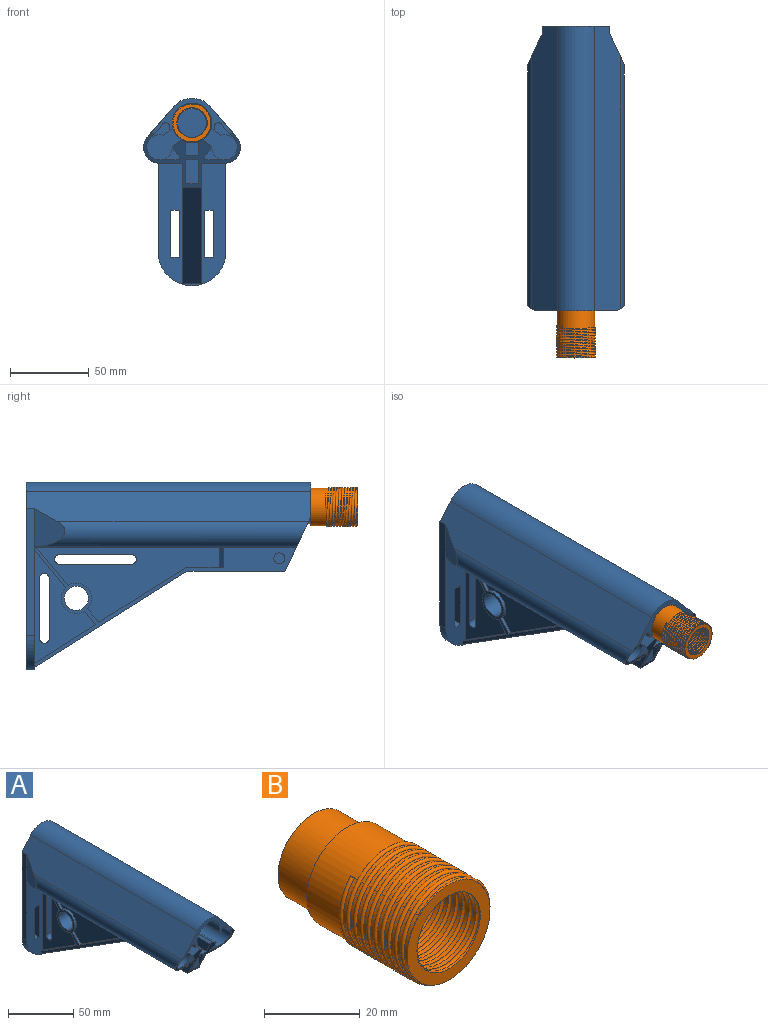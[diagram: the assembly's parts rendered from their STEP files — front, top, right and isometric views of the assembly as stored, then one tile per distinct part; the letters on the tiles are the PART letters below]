
ASSEMBLY  parts=2 mates=1
PART A: 102 faces, bbox 61.2x180.1x118.6 mm
  f0: plane 77.59x43mm, normal (0,-1,0), area 2194mm2, adj f4,f8,f9,f10,f11,f12,f15,f23
  f1: plane 118.58x43mm, normal (0,1,0), area 4330mm2, adj f13,f14,f22,f23,f24,f25,f94,f95
  f2: plane 8.42x6.86mm, normal (0,0.78,-0.63), area 21.7mm2, adj f9,f33,f34,f68
  f3: plane 8.58x7.16mm, normal (0,-0.77,0.64), area 22.3mm2, adj f9,f37,f39,f67
  f4: plane 24.44x19.89mm, normal (0,0.78,-0.63), area 63mm2, adj f0,f8,f42,f66
  f5: plane 24.33x20.29mm, normal (0,-0.77,0.64), area 63.4mm2, adj f8,f10,f47,f65
  f6: plane 61.22x34.25mm, normal (0,-0.9,-0.43), area 463mm2, adj f7,f8,f9,f10,f11,f12,f13,f14
  f7: cylinder r=8mm len=148.25mm, axis (0,1,0), area 5825.9mm2, adj f6,f48,f51,f55,f56,f88,f89
  f8: plane 166.01x76.2mm, normal (-1,0,0), area 1146.1mm2, adj f0,f4,f5,f6,f10,f21,f31,f40
  f9: plane 166.01x76.2mm, normal (1,0,0), area 1184.3mm2, adj f0,f2,f3,f6,f11,f21,f31,f32
  f10: plane 166.01x16.61mm, normal (0,0,-1), area 2659.9mm2, adj f0,f5,f6,f8,f15,f47,f91
  f11: plane 166.01x16.61mm, normal (0,0,-1), area 2659.9mm2, adj f0,f6,f9,f12,f38,f39,f90
  f12: cylinder r=10mm len=173.87mm, axis (0,1,0), area 3544.9mm2, adj f0,f6,f11,f13,f29
  f13: plane 180.08x18.88mm, normal (0.76,0,0.65), area 4349.5mm2, adj f1,f6,f12,f20,f22,f25,f29,f30
  f14: plane 180.08x18.88mm, normal (-0.76,0,0.65), area 4349.5mm2, adj f1,f6,f15,f20,f22,f24,f27
  f15: cylinder r=10mm len=173.87mm, axis (0,1,0), area 3544.9mm2, adj f0,f6,f10,f14,f27
  f16: plane 172.59x8.74mm, normal (1,0,0), area 1490.5mm2, adj f6,f17,f19,f26
  f17: cylinder r=12.25mm len=175mm, axis (0,1,0), area 9267mm2, adj f6,f16,f18,f20,f26,f48,f50,f86
  f18: plane 172.59x8.74mm, normal (-1,0,0), area 1490.5mm2, adj f6,f17,f19,f26
  f19: plane 168.43x8mm, normal (0,0,1), area 1299.7mm2, adj f6,f16,f18,f26,f72
  f20: plane 52.33x22.14mm, normal (0,-1,0), area 237.4mm2, adj f6,f13,f14,f17,f22,f54,f55,f57
  f21: plane 61.93x12mm, normal (0,0,-1), area 730.6mm2, adj f6,f8,f9,f31,f70
  f22: cylinder r=15.63mm len=180.08mm, axis (0,1,0), area 4940.3mm2, adj f1,f13,f14,f20
  f23: cylinder r=21.5mm len=43mm, axis (0,-1,0), area 343.1mm2, adj f0,f1,f24,f25
  f24: plane 80.38x5.08mm, normal (-1,0,0), area 408.3mm2, adj f0,f1,f14,f23,f27
  f25: plane 80.38x5.08mm, normal (1,0,0), area 404.2mm2, adj f0,f1,f13,f23,f28,f30
  f26: plane 32.57x24.5mm, normal (0,-1,0), area 537.8mm2, adj f16,f17,f18,f19
  f27: plane 24.29x19.54mm, normal (-0.91,0.42,0), area 355.4mm2, adj f14,f15,f24
  f28: plane 0.17x0.07mm, normal (0,0,1), area 0mm2, adj f25,f29,f30
  f29: plane 24.4x19.68mm, normal (0.91,0.42,0), area 359.2mm2, adj f0,f12,f13,f28,f30
  f30: plane 24.4x0.07mm, normal (0.42,-0.91,0), area 1.8mm2, adj f13,f25,f28,f29
  f31: plane 96.76x60.84mm, normal (0,-0.53,-0.85), area 1371.6mm2, adj f0,f8,f9,f21
  f32: plane 24.44x19.89mm, normal (0,0.78,-0.63), area 63mm2, adj f0,f9,f34,f68
  f33: plane 38.85x24.67mm, normal (0,0.54,0.84), area 92mm2, adj f0,f2,f9,f34
  f34: plane 72.39x38.85mm, normal (1,0,0), area 1021.4mm2, adj f0,f2,f32,f33,f68,f77,f78,f79
  f35: plane 22.84x2mm, normal (0,0,1), area 43.7mm2, adj f9,f36,f39,f90
  f36: plane 16.91x10.14mm, normal (0,0.51,0.86), area 39.4mm2, adj f9,f35,f37,f39
  f37: plane 38.85x24.67mm, normal (0,0.54,0.84), area 92mm2, adj f3,f9,f36,f39
  f38: plane 24.33x20.29mm, normal (0,-0.77,0.64), area 63.4mm2, adj f9,f11,f39,f67
  f39: plane 116.33x47.63mm, normal (1,0,0), area 2452.7mm2, adj f3,f11,f35,f36,f37,f38,f67,f73
  f40: plane 38.85x24.67mm, normal (0,0.54,0.84), area 92mm2, adj f0,f8,f41,f42
  f41: plane 8.42x6.86mm, normal (0,0.78,-0.63), area 21.7mm2, adj f8,f40,f42,f66
  f42: plane 72.39x38.85mm, normal (-1,0,0), area 1021.4mm2, adj f0,f4,f40,f41,f66,f77,f78,f79
  f43: plane 38.85x24.67mm, normal (0,0.54,0.84), area 92mm2, adj f8,f44,f46,f47
  f44: plane 16.91x10.14mm, normal (0,0.51,0.86), area 39.4mm2, adj f8,f43,f45,f47
  f45: plane 22.84x2mm, normal (0,0,1), area 43.7mm2, adj f8,f44,f47,f91
  f46: plane 8.58x7.16mm, normal (0,-0.77,0.64), area 22.3mm2, adj f8,f43,f47,f65
  f47: plane 116.33x47.63mm, normal (-1,0,0), area 2452.7mm2, adj f5,f10,f43,f44,f45,f46,f65,f73
  f48: plane 22.18x20.19mm, normal (0,-1,0), area 256.9mm2, adj f7,f17,f88,f89
  f49: cylinder r=8mm len=148.25mm, axis (0,1,0), area 5825.9mm2, adj f6,f50,f58,f61,f63,f86,f87
  f50: plane 22.18x20.19mm, normal (0,-1,0), area 256.9mm2, adj f17,f49,f86,f87
  f51: plane 12.79x10.33mm, normal (0,-1,0), area 49.1mm2, adj f7,f54,f55,f57,f88
  f52: plane 2.49x1.18mm, normal (1,0,0), area 1.5mm2, adj f6,f53,f56
  f53: cylinder r=11.9mm len=5.9mm, axis (0,-1,0), area 18.5mm2, adj f6,f52,f56,f89
  f54: plane 8x2.55mm, normal (0.99,0,-0.12), area 20.5mm2, adj f20,f51,f57,f88
  f55: plane 9.47x8.11mm, normal (-0.76,0,-0.65), area 95.5mm2, adj f6,f7,f20,f51,f57
  f56: plane 11.34x8.39mm, normal (0,-1,0), area 35.2mm2, adj f6,f7,f52,f53,f89
  f57: cylinder r=2.48mm len=8mm, axis (0,-1,0), area 47.3mm2, adj f20,f51,f54,f55
  f58: plane 11.34x8.39mm, normal (0,-1,0), area 35.2mm2, adj f6,f49,f59,f60,f87
  f59: cylinder r=11.9mm len=5.9mm, axis (0,-1,0), area 18.5mm2, adj f6,f58,f60,f87
  f60: plane 2.49x1.18mm, normal (-1,0,0), area 1.5mm2, adj f6,f58,f59
  f61: plane 9.47x8.11mm, normal (0.76,0,-0.65), area 95.5mm2, adj f6,f20,f49,f63,f64
  f62: plane 8x2.55mm, normal (-0.99,0,-0.12), area 20.5mm2, adj f20,f63,f64,f86
  f63: plane 12.79x10.33mm, normal (0,-1,0), area 49.1mm2, adj f49,f61,f62,f64,f86
  f64: cylinder r=2.48mm len=8mm, axis (0,-1,0), area 47.3mm2, adj f20,f61,f62,f63
  f65: cylinder r=9.65mm len=16.29mm, axis (-1,0,0), area 56.1mm2, adj f5,f8,f46,f47
  f66: cylinder r=9.65mm len=16.36mm, axis (-1,0,0), area 56.1mm2, adj f4,f8,f41,f42
  f67: cylinder r=9.65mm len=16.29mm, axis (-1,0,0), area 56.1mm2, adj f3,f9,f38,f39
  f68: cylinder r=9.65mm len=16.36mm, axis (-1,0,0), area 56.1mm2, adj f2,f9,f32,f34
  f69: cylinder r=7.62mm len=15.24mm, axis (-1,0,0), area 574.5mm2, adj f8,f9
  f70: cylinder r=2mm len=5mm, axis (0,0,-1), area 62.8mm2, adj f21,f71
  f71: plane 7.8x7.8mm, normal (0,0,1), area 35.2mm2, adj f70,f72
  f72: cylinder r=3.9mm len=15.44mm, axis (0,0,-1), area 378.2mm2, adj f19,f71
  f73: cylinder r=3.07mm len=8mm, axis (-1,0,0), area 77.1mm2, adj f39,f47,f74,f76
  f74: plane 45.72x8mm, normal (0,0,-1), area 365.8mm2, adj f39,f47,f73,f75
  f75: cylinder r=3.07mm len=8mm, axis (-1,0,0), area 77.1mm2, adj f39,f47,f74,f76
  f76: plane 45.72x8mm, normal (0,0,1), area 365.8mm2, adj f39,f47,f73,f75
  f77: cylinder r=3.04mm len=8mm, axis (-1,0,0), area 76.5mm2, adj f34,f42,f78,f80
  f78: plane 38.05x8mm, normal (0,1,0), area 304.4mm2, adj f34,f42,f77,f79
  f79: cylinder r=3.04mm len=8mm, axis (-1,0,0), area 76.5mm2, adj f34,f42,f78,f80
  f80: plane 38.05x8mm, normal (0,-1,0), area 304.4mm2, adj f34,f42,f77,f79
  f81: plane 15.03x7.25mm, normal (-1,0,0), area 55.1mm2, adj f6,f82,f84,f85
  f82: plane 8x0.09mm, normal (0,0,1), area 0.7mm2, adj f6,f81,f83,f85
  f83: plane 15.03x7.25mm, normal (1,0,0), area 55.1mm2, adj f6,f82,f84,f85
  f84: plane 8x7.25mm, normal (0,0,-1), area 58mm2, adj f6,f81,f83,f85
  f85: plane 15.03x8mm, normal (0,-1,0), area 120.2mm2, adj f81,f82,f83,f84
  f86: plane 150x6.18mm, normal (0.6,0,-0.8), area 1116.9mm2, adj f17,f20,f49,f50,f62,f63
  f87: plane 148.14x6.18mm, normal (-0.6,0,0.8), area 1134.3mm2, adj f6,f17,f49,f50,f58,f59
  f88: plane 150x6.18mm, normal (-0.6,0,-0.8), area 1116.9mm2, adj f7,f17,f20,f48,f51,f54
  f89: plane 148.14x6.18mm, normal (0.6,0,0.8), area 1134.3mm2, adj f6,f7,f17,f48,f53,f56
  f90: plane 12.82x2mm, normal (0.71,0.71,0), area 36.3mm2, adj f9,f11,f35,f39
  f91: plane 12.82x2mm, normal (-0.71,0.71,0), area 36.3mm2, adj f8,f10,f45,f47
  f92: cylinder r=3.49mm len=6.98mm, axis (-1,0,0), area 2.2mm2, adj f8,f93
  f93: plane 6.98x6.98mm, normal (-1,0,0), area 38.3mm2, adj f92
  f94: plane 5.36x5.08mm, normal (0,0,1), area 27.2mm2, adj f0,f1,f95,f97
  f95: plane 29.62x5.08mm, normal (-1,0,0), area 150.5mm2, adj f0,f1,f94,f96
  f96: plane 5.36x5.08mm, normal (0,0,-1), area 27.2mm2, adj f0,f1,f95,f97
  f97: plane 29.62x5.08mm, normal (1,0,0), area 150.5mm2, adj f0,f1,f94,f96
  f98: plane 5.36x5.08mm, normal (0,0,1), area 27.2mm2, adj f0,f1,f99,f101
  f99: plane 29.62x5.08mm, normal (-1,0,0), area 150.5mm2, adj f0,f1,f98,f100
  f100: plane 5.36x5.08mm, normal (0,0,-1), area 27.2mm2, adj f0,f1,f99,f101
  f101: plane 29.62x5.08mm, normal (1,0,0), area 150.5mm2, adj f0,f1,f98,f100
PART B: 31 faces, bbox 25.2x41.3x25.2 mm
  f0: plane 24x24mm, normal (0,1,0), area 106mm2, adj f2,f30
  f1: plane 24.71x24.71mm, normal (0,-1,0), area 194.4mm2, adj f12,f13,f26,f28
  f2: cylinder r=12mm len=24mm, axis (0,1,0), area 791.7mm2, adj f0,f3,f27,f28
  f3: cylinder r=12mm len=24mm, axis (0,1,0), area 75.4mm2, adj f2,f4,f28
  f4: cylinder r=12mm len=24mm, axis (0,1,0), area 75.4mm2, adj f3,f5,f28
  f5: cylinder r=12mm len=24mm, axis (0,1,0), area 75.4mm2, adj f4,f6,f28
  f6: cylinder r=12mm len=24mm, axis (0,1,0), area 75.4mm2, adj f5,f7,f28
  f7: cylinder r=12mm len=24mm, axis (0,1,0), area 75.4mm2, adj f6,f8,f28
  f8: cylinder r=12mm len=24mm, axis (0,1,0), area 75.4mm2, adj f7,f9,f28
  f9: cylinder r=12mm len=24mm, axis (0,1,0), area 75.4mm2, adj f8,f10,f28
  f10: cylinder r=12mm len=24mm, axis (0,1,0), area 75.4mm2, adj f9,f11,f28
  f11: cylinder r=12mm len=24mm, axis (0,1,0), area 75.4mm2, adj f10,f12,f28
  f12: cylinder r=12mm len=24mm, axis (0,1,0), area 37.7mm2, adj f1,f11,f28
  f13: cylinder r=9.12mm len=18.25mm, axis (0,1,0), area 21.5mm2, adj f1,f14,f26
  f14: cylinder r=9.12mm len=18.25mm, axis (0,1,0), area 57.3mm2, adj f13,f15,f26
  f15: cylinder r=9.12mm len=18.25mm, axis (0,1,0), area 57.3mm2, adj f14,f16,f26
  f16: cylinder r=9.12mm len=18.25mm, axis (0,1,0), area 57.3mm2, adj f15,f17,f26
  f17: cylinder r=9.12mm len=18.25mm, axis (0,1,0), area 57.3mm2, adj f16,f18,f26
  f18: cylinder r=9.12mm len=18.25mm, axis (0,1,0), area 57.3mm2, adj f17,f19,f26
  f19: cylinder r=9.12mm len=18.25mm, axis (0,1,0), area 57.3mm2, adj f18,f20,f26
  f20: cylinder r=9.12mm len=18.25mm, axis (0,1,0), area 57.3mm2, adj f19,f21,f26
  f21: cylinder r=9.12mm len=18.25mm, axis (0,1,0), area 57.3mm2, adj f20,f22,f26
  f22: cylinder r=9.12mm len=18.25mm, axis (0,1,0), area 57.3mm2, adj f21,f23,f26
  f23: cylinder r=9.12mm len=18.25mm, axis (0,1,0), area 57.3mm2, adj f22,f24,f26
  f24: cylinder r=9.12mm len=19.75mm, axis (0,1,0), area 1067.8mm2, adj f23,f25,f26,f29
  f25: plane 1.14x0.51mm, normal (-0.71,-0.03,-0.71), area 0.4mm2, adj f24,f26
  f26: bspline ~23.5x19.25mm, area 1025.4mm2, adj f1,f13,f14,f15,f16,f17,f18,f19
  f27: plane 1x0.36mm, normal (0.71,0.03,0.71), area 0.4mm2, adj f2,f28
  f28: bspline ~24.97x24.96mm, area 1215.7mm2, adj f1,f2,f3,f4,f5,f6,f7,f8
  f29: plane 21x21mm, normal (0,1,0), area 84.8mm2, adj f24,f30
  f30: cylinder r=10.5mm len=21mm, axis (0,-1,0), area 659.7mm2, adj f0,f29
PLACE A t=(-14.48,26.05,51.62)mm
PLACE B t=(-14.48,-8.95,77.02)mm
MATE fastened B.f2 <-> A.f17  axis (0,1,0) through (-14.48,-148.95,77.02)mm
